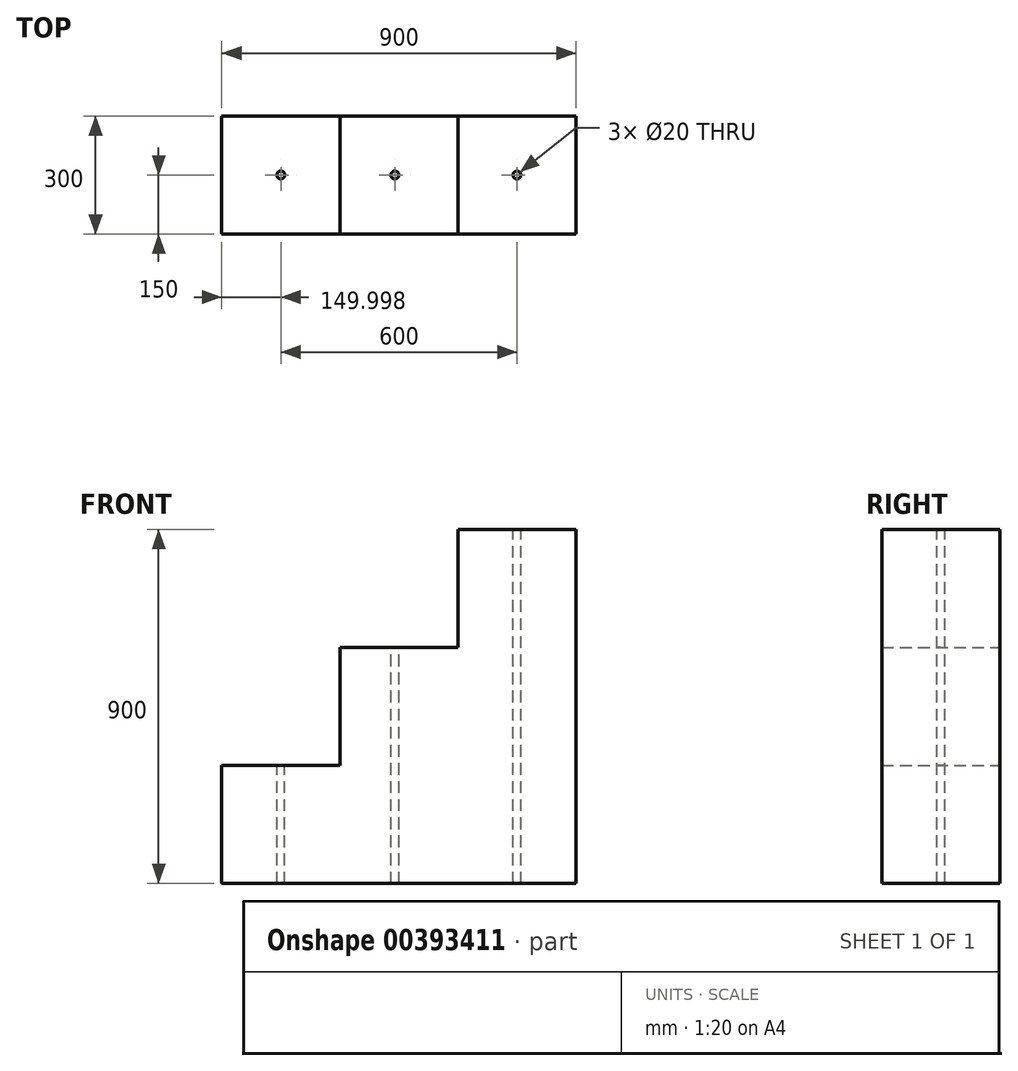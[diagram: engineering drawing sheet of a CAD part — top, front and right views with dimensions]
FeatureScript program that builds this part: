
annotation { "Feature Type Name" : "Feature", "Feature Type Description" : "" }
export const myFeature = defineFeature(function(context is Context, id is Id, definition is map)
    precondition{}
    {
        {
            var Q0;
            Q0=qCreatedBy(makeId("Front.planeOp"),FACE);
            var sketch = newSketch(context, id + "F0", { "sketchPlane" : qUnion([Q0])});
            skLineSegment(sketch, "E0", {"start": v(460.32, -440.07) * mm, "end": v(460.32, 459.93) * mm});
            skLineSegment(sketch, "E1", {"start": v(460.32, 459.93) * mm, "end": v(160.32, 459.93) * mm});
            skLineSegment(sketch, "E2", {"start": v(160.32, 459.93) * mm, "end": v(160.32, 159.93) * mm});
            skLineSegment(sketch, "E3", {"start": v(160.32, 159.93) * mm, "end": v(-139.68, 159.93) * mm});
            skLineSegment(sketch, "E4", {"start": v(-139.68, 159.93) * mm, "end": v(-139.68, -140.07) * mm});
            skLineSegment(sketch, "E5", {"start": v(-139.68, -140.07) * mm, "end": v(-439.68, -140.07) * mm});
            skLineSegment(sketch, "E6", {"start": v(-439.68, -140.07) * mm, "end": v(-439.68, -440.07) * mm});
            skLineSegment(sketch, "E7", {"start": v(-439.68, -440.07) * mm, "end": v(460.32, -440.07) * mm});
            skSolve(sketch);
        }
        {
            var Q0;
            Q0 = qSketchRegion(id + "F0", true);
            extrude(context, id + "F1", {"entities" : qUnion([Q0]), "depth" : 300 * mm});
        }
        {
            var Q0;
            Q0=makeQuery(id+"F1.opExtrude","SWEPT_FACE",FACE,{"disambiguationData":[OSD([sQuery(id+"F0.wireOp",EDGE,"E1")])]});
            var sketch = newSketch(context, id + "F2", { "sketchPlane" : qUnion([Q0])});
            skCircle(sketch, "E8", {"center": v(310.32, -150) * mm, "radius": 10 * mm});
            skPoint(sketch, "E8.centerSnap0", {"position": v(160.32, -150) * mm});
            skPoint(sketch, "E8.centerSnap1", {"position": v(310.32, 0) * mm});
            skCircle(sketch, "E9", {"center": v(0, -150) * mm, "radius": 10 * mm});
            skSolve(sketch);
        }
        {
            var Q0;
            Q0 = qSketchRegion(id + "F2", true);
            extrude(context, id + "F3", {"entities" : qUnion([Q0]), "operationType" : NewBodyOperationType.REMOVE, "endBound" : BoundingType.THROUGH_ALL, "oppositeDirection" : true, "depth" : 25 * mm});
        }
        {
            var Q0;
            Q0=makeQuery(id+"F1.opExtrude","SWEPT_FACE",FACE,{"disambiguationData":[OSD([sQuery(id+"F0.wireOp",EDGE,"E5")])]});
            var sketch = newSketch(context, id + "F4", { "sketchPlane" : qUnion([Q0])});
            skCircle(sketch, "E10", {"center": v(-289.68, -150) * mm, "radius": 10 * mm});
            skPoint(sketch, "E10.centerSnap0", {"position": v(-139.68, -150) * mm});
            skPoint(sketch, "E10.centerSnap1", {"position": v(-289.68, 0) * mm});
            skSolve(sketch);
        }
        {
            var Q0;
            Q0 = qSketchRegion(id + "F4", true);
            extrude(context, id + "F5", {"entities" : qUnion([Q0]), "operationType" : NewBodyOperationType.REMOVE, "endBound" : BoundingType.THROUGH_ALL, "oppositeDirection" : true, "depth" : 25 * mm});
        }
    });
